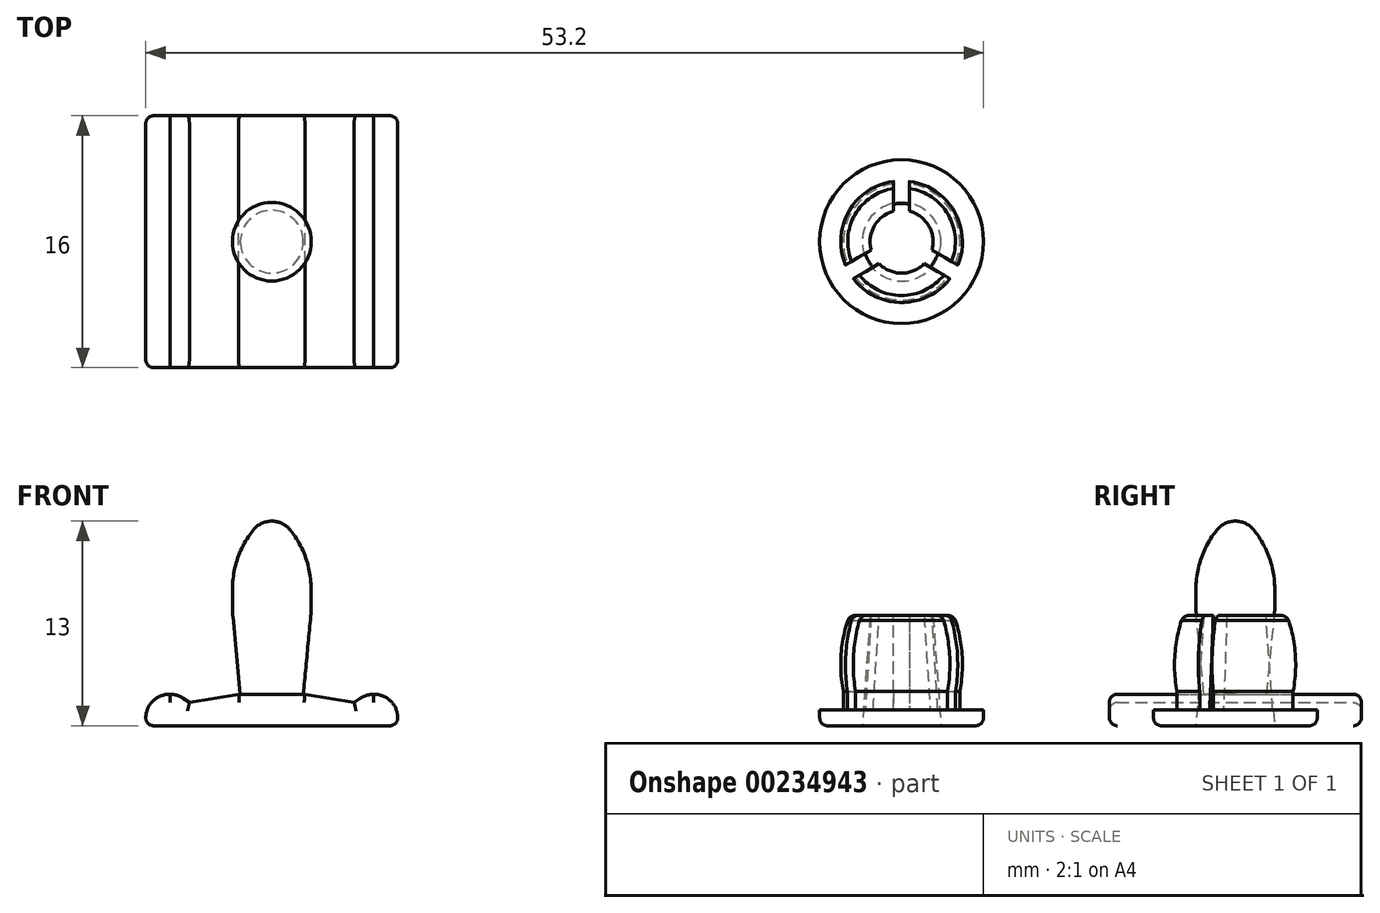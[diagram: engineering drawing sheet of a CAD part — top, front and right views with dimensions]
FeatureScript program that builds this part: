
annotation { "Feature Type Name" : "Feature", "Feature Type Description" : "" }
export const myFeature = defineFeature(function(context is Context, id is Id, definition is map)
    precondition{}
    {
        {
            var Q0;
            Q0=qCreatedBy(makeId("Front.planeOp"),FACE);
            var sketch = newSketch(context, id + "F0", { "sketchPlane" : qUnion([Q0])});
            skLineSegment(sketch, "E0", {"start": v(0, 0) * mm, "end": v(8, 0) * mm});
            skLineSegment(sketch, "E1", {"start": v(8, 0) * mm, "end": v(8, 0.5) * mm});
            skLineSegment(sketch, "E2", {"start": v(5.62, 1.74) * mm, "end": v(5.23, 1.48) * mm});
            skLineSegment(sketch, "E3", {"start": v(5.23, 1.48) * mm, "end": v(2.1, 2) * mm});
            skLineSegment(sketch, "E4", {"start": v(2.1, 2) * mm, "end": v(0, 2) * mm});
            skPoint(sketch, "E5.visualSharp", {"position": v(8, 2) * mm});
            skArc(sketch, "E5.filletArc", {"start": v(8, 0.5) * mm, "mid": v(7.55, 1.57) * mm, "end": v(6.46, 2) * mm});
            skPoint(sketch, "E6.visualSharp", {"position": v(6, 2) * mm});
            skArc(sketch, "E6.filletArc", {"start": v(6.46, 2) * mm, "mid": v(6.02, 1.93) * mm, "end": v(5.62, 1.74) * mm});
            skLineSegment(sketch, "E7.MirrorCS", {"start": v(0, 0) * mm, "end": v(-8, 0) * mm});
            skLineSegment(sketch, "E8.MirrorCS", {"start": v(-8, 0) * mm, "end": v(-8, 0.5) * mm});
            skArc(sketch, "E9.MirrorCS", {"start": v(-8, 0.5) * mm, "mid": v(-7.55, 1.57) * mm, "end": v(-6.46, 2) * mm});
            skArc(sketch, "E10.MirrorCS", {"start": v(-6.46, 2) * mm, "mid": v(-6.02, 1.93) * mm, "end": v(-5.62, 1.74) * mm});
            skLineSegment(sketch, "E11.MirrorCS", {"start": v(-5.62, 1.74) * mm, "end": v(-5.23, 1.48) * mm});
            skLineSegment(sketch, "E12.MirrorCS", {"start": v(-5.23, 1.48) * mm, "end": v(-2.1, 2) * mm});
            skLineSegment(sketch, "E13.MirrorCS", {"start": v(-2.1, 2) * mm, "end": v(0, 2) * mm});
            skSolve(sketch);
        }
        {
            var Q0;
            Q0=qCreatedBy(makeId("Front.planeOp"),FACE);
            var sketch = newSketch(context, id + "F1", { "sketchPlane" : qUnion([Q0])});
            skPoint(sketch, "E14.0", {"position": v(0, 2) * mm});
            skLineSegment(sketch, "E15", {"start": v(0, 2) * mm, "end": v(2, 2) * mm});
            skLineSegment(sketch, "E16", {"start": v(2, 2) * mm, "end": v(2.47, 6.95) * mm});
            skLineSegment(sketch, "E17", {"start": v(2.5, 7.52) * mm, "end": v(2.5, 8.67) * mm});
            skLineSegment(sketch, "E18", {"start": v(1.28, 12.29) * mm, "end": v(1.2, 12.4) * mm});
            skLineSegment(sketch, "E19", {"start": v(0, 13) * mm, "end": v(0, 13) * mm});
            skLineSegment(sketch, "E20", {"start": v(0, 13) * mm, "end": v(0, 2) * mm});
            skPoint(sketch, "E21.visualSharp", {"position": v(0.75, 13) * mm});
            skArc(sketch, "E21.filletArc", {"start": v(1.2, 12.4) * mm, "mid": v(0.67, 12.84) * mm, "end": v(0, 13) * mm});
            skPoint(sketch, "E22.visualSharp", {"position": v(2.5, 10.68) * mm});
            skArc(sketch, "E22.filletArc", {"start": v(2.5, 8.67) * mm, "mid": v(2.19, 10.58) * mm, "end": v(1.28, 12.29) * mm});
            skPoint(sketch, "E23.visualSharp", {"position": v(2.5, 7.24) * mm});
            skArc(sketch, "E23.filletArc", {"start": v(2.47, 6.95) * mm, "mid": v(2.5, 7.24) * mm, "end": v(2.5, 7.52) * mm});
            skSolve(sketch);
        }
        {
            var Q0;
            Q0 = qSketchRegion(id + "F0", true);
            extrude(context, id + "F2", {"entities" : qUnion([Q0]), "endBound" : BoundingType.SYMMETRIC, "depth" : 16 * mm});
        }
        {
            var Q0;
            Q0 = qSketchRegion(id + "F1", true);
            var Q1;
            Q1=sQuery(id+"F1.wireOp",EDGE,"E20");
            revolve(context, id + "F3", {"operationType" : NewBodyOperationType.ADD, "entities" : qUnion([Q0]), "axis" : qUnion([Q1]), "revolveType" : RevolveType.FULL});
        }
        {
            var Q0;
            Q0=makeQuery(id+"F2.opExtrude","CAP_FACE",FACE,{"disambiguationData":[OSD([sQuery(id+"F0.wireOp",EDGE,"E0"),sQuery(id+"F0.wireOp",EDGE,"E1"),sQuery(id+"F0.wireOp",EDGE,"E2"),sQuery(id+"F0.wireOp",EDGE,"E3"),sQuery(id+"F0.wireOp",EDGE,"E4"),sQuery(id+"F0.wireOp",EDGE,"E5.filletArc"),sQuery(id+"F0.wireOp",EDGE,"E6.filletArc"),sQuery(id+"F0.wireOp",EDGE,"E7.MirrorCS"),sQuery(id+"F0.wireOp",EDGE,"E8.MirrorCS"),sQuery(id+"F0.wireOp",EDGE,"E9.MirrorCS"),sQuery(id+"F0.wireOp",EDGE,"E10.MirrorCS"),sQuery(id+"F0.wireOp",EDGE,"E11.MirrorCS"),sQuery(id+"F0.wireOp",EDGE,"E12.MirrorCS"),sQuery(id+"F0.wireOp",EDGE,"E13.MirrorCS")])],"isStart":false});
            var Q1;
            Q1=makeQuery(id+"F2.opExtrude","CAP_FACE",FACE,{"disambiguationData":[OSD([sQuery(id+"F0.wireOp",EDGE,"E0"),sQuery(id+"F0.wireOp",EDGE,"E1"),sQuery(id+"F0.wireOp",EDGE,"E2"),sQuery(id+"F0.wireOp",EDGE,"E3"),sQuery(id+"F0.wireOp",EDGE,"E4"),sQuery(id+"F0.wireOp",EDGE,"E5.filletArc"),sQuery(id+"F0.wireOp",EDGE,"E6.filletArc"),sQuery(id+"F0.wireOp",EDGE,"E7.MirrorCS"),sQuery(id+"F0.wireOp",EDGE,"E8.MirrorCS"),sQuery(id+"F0.wireOp",EDGE,"E9.MirrorCS"),sQuery(id+"F0.wireOp",EDGE,"E10.MirrorCS"),sQuery(id+"F0.wireOp",EDGE,"E11.MirrorCS"),sQuery(id+"F0.wireOp",EDGE,"E12.MirrorCS"),sQuery(id+"F0.wireOp",EDGE,"E13.MirrorCS")])],"isStart":true});
            var Q2;
            Q2=makeQuery(id+"F2.opExtrude","SWEPT_EDGE",EDGE,{"disambiguationData":[OSD([sQuery(id+"F0.wireOp",EDGE,"E7.MirrorCS"),sQuery(id+"F0.wireOp",EDGE,"E8.MirrorCS")])]});
            var Q3;
            Q3=makeQuery(id+"F2.opExtrude","SWEPT_EDGE",EDGE,{"disambiguationData":[OSD([sQuery(id+"F0.wireOp",EDGE,"E0"),sQuery(id+"F0.wireOp",EDGE,"E1")])]});
            var Q4;
            Q4=makeQuery(id+"F3.opRevolve","SWEPT_EDGE",EDGE,{"disambiguationData":[OSD([sQuery(id+"F1.wireOp",EDGE,"E15"),sQuery(id+"F1.wireOp",EDGE,"E16")])]});
            fillet(context, id + "F4", {"entities" : qUnion([Q0, Q1, Q2, Q3, Q4]), "radius" : .5 * mm, "tangentPropagation" : true, "allowEdgeOverflow" : false});
        }
        {
            var Q0;
            Q0=qCreatedBy(makeId("Front.planeOp"),FACE);
            var sketch = newSketch(context, id + "F5", { "sketchPlane" : qUnion([Q0])});
            skLineSegment(sketch, "E24", {"start": v(0, 0) * mm, "end": v(40, 0) * mm, "construction": true});
            skLineSegment(sketch, "E25", {"start": v(40, 0) * mm, "end": v(40, 7) * mm});
            skLineSegment(sketch, "E26", {"start": v(40, 0) * mm, "end": v(42.5, 0) * mm, "construction": true});
            skLineSegment(sketch, "E27", {"start": v(42.5, 0) * mm, "end": v(44.7, 0) * mm});
            skLineSegment(sketch, "E28", {"start": v(45.2, 0.5) * mm, "end": v(45.2, 1) * mm});
            skLineSegment(sketch, "E29", {"start": v(45.2, 1) * mm, "end": v(43.7, 1) * mm});
            skPoint(sketch, "E30.visualSharp", {"position": v(44.17, 4.43) * mm});
            skArc(sketch, "E30.filletArc", {"start": v(43.7, 2.18) * mm, "mid": v(43.85, 4.45) * mm, "end": v(43.42, 6.68) * mm});
            skPoint(sketch, "E31.visualSharp", {"position": v(43.2, 7) * mm});
            skArc(sketch, "E31.filletArc", {"start": v(43.42, 6.68) * mm, "mid": v(43.24, 6.92) * mm, "end": v(42.95, 7) * mm});
            skPoint(sketch, "E32.visualSharp", {"position": v(45.2, 0) * mm});
            skArc(sketch, "E32.filletArc", {"start": v(44.7, 0) * mm, "mid": v(45.05, 0.15) * mm, "end": v(45.2, 0.5) * mm});
            skLineSegment(sketch, "E33", {"start": v(42.5, 0) * mm, "end": v(42, 7) * mm});
            skLineSegment(sketch, "E34", {"start": v(42.95, 7) * mm, "end": v(42, 7) * mm});
            skLineSegment(sketch, "E35", {"start": v(43.7, 1) * mm, "end": v(43.7, 2.18) * mm});
            skSolve(sketch);
        }
        {
            var Q0;
            Q0=makeQuery(id+"F5.imprint","IMPRINT",FACE,{"disambiguationData":[TD([[makeQuery(id+"F5.imprint","IMPRINT",EDGE,{"derivedFrom":sQuery(id+"F5.wireOp",EDGE,"E27")}),1.0]])]});
            var Q1;
            Q1=sQuery(id+"F5.wireOp",EDGE,"E25");
            revolve(context, id + "F6", {"entities" : qUnion([Q0]), "axis" : qUnion([Q1]), "revolveType" : RevolveType.FULL});
        }
        {
            var Q0;
            Q0=makeQuery(id+"F6.opRevolve","SWEPT_FACE",FACE,{"disambiguationData":[OSD([sQuery(id+"F5.wireOp",EDGE,"E29")])]});
            var sketch = newSketch(context, id + "F7", { "sketchPlane" : qUnion([Q0])});
            skLineSegment(sketch, "E36", {"start": v(39.5, 0) * mm, "end": v(39.5, 8.54) * mm});
            skLineSegment(sketch, "E37", {"start": v(39.5, 8.54) * mm, "end": v(40.5, 8.54) * mm});
            skLineSegment(sketch, "E38", {"start": v(40.5, 8.54) * mm, "end": v(40.5, 0) * mm});
            skLineSegment(sketch, "E39.1.0", {"start": v(40.25, -0.43) * mm, "end": v(32.85, -4.7) * mm});
            skLineSegment(sketch, "E39.1.1", {"start": v(32.35, -3.84) * mm, "end": v(39.75, 0.43) * mm});
            skLineSegment(sketch, "E39.1.2", {"start": v(32.85, -4.7) * mm, "end": v(32.35, -3.84) * mm});
            skLineSegment(sketch, "E39.2.0", {"start": v(40.25, 0.43) * mm, "end": v(47.65, -3.84) * mm});
            skLineSegment(sketch, "E39.2.1", {"start": v(47.15, -4.7) * mm, "end": v(39.75, -0.43) * mm});
            skLineSegment(sketch, "E39.2.2", {"start": v(47.65, -3.84) * mm, "end": v(47.15, -4.7) * mm});
            skPoint(sketch, "E39.center", {"position": v(40, 0) * mm});
            skSolve(sketch);
        }
        {
            var Q0;
            Q0 = qSketchRegion(id + "F7", true);
            extrude(context, id + "F8", {"entities" : qUnion([Q0]), "operationType" : NewBodyOperationType.REMOVE, "depth" : 7.1 * mm});
        }
    });
